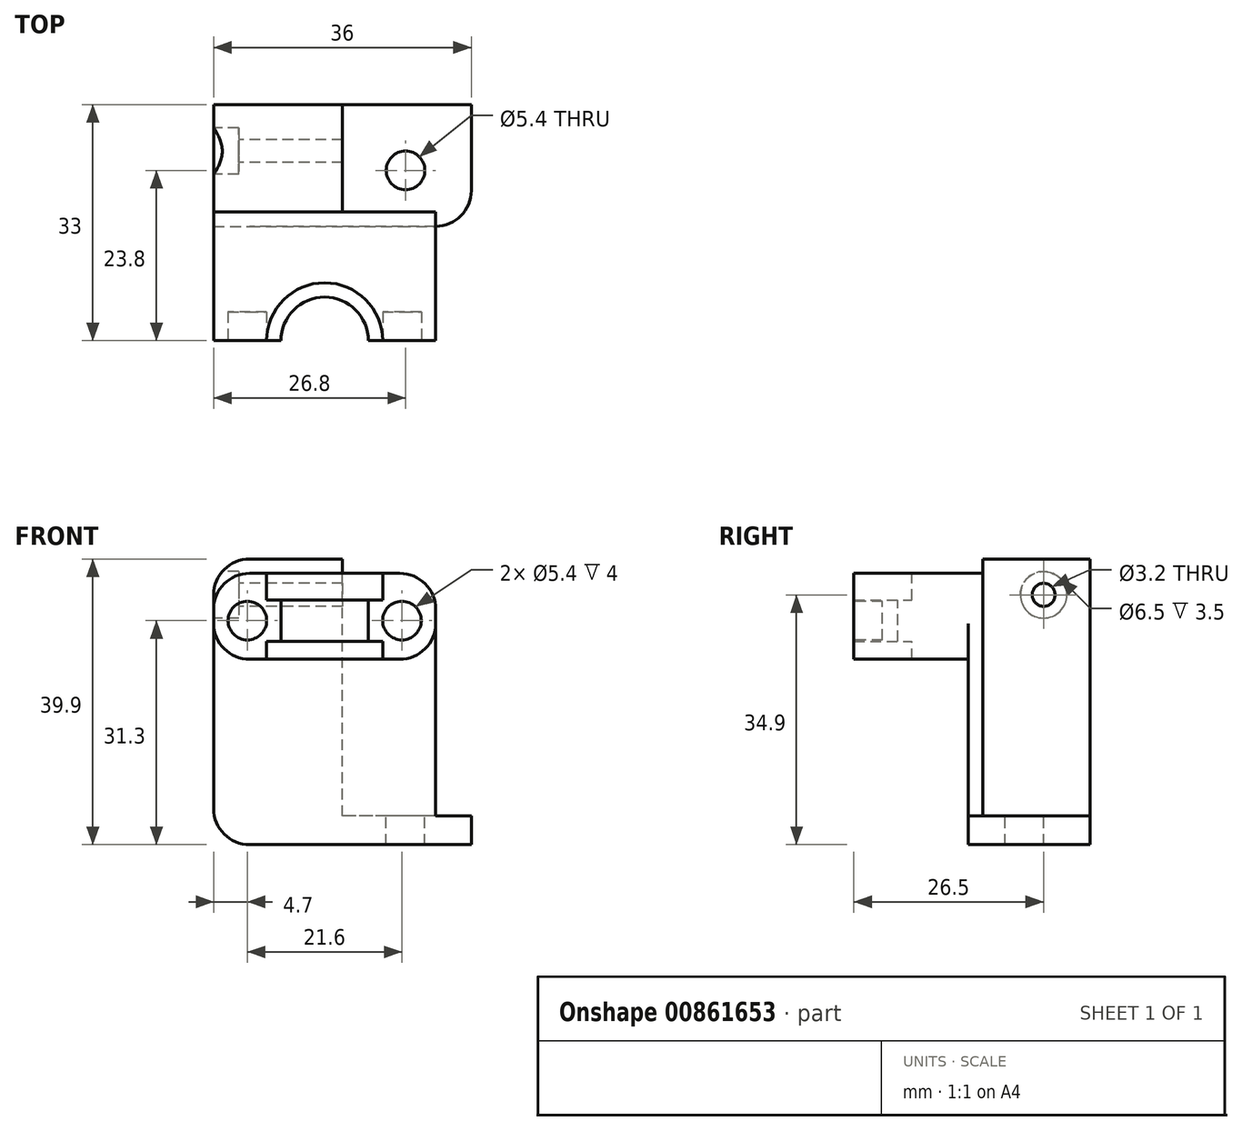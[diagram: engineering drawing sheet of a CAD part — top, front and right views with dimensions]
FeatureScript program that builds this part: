
annotation { "Feature Type Name" : "Feature", "Feature Type Description" : "" }
export const myFeature = defineFeature(function(context is Context, id is Id, definition is map)
    precondition{}
    {
        {
            var Q0;
            Q0=qCreatedBy(makeId("Front.planeOp"),FACE);
            var sketch = newSketch(context, id + "F0", { "sketchPlane" : qUnion([Q0])});
            skLineSegment(sketch, "E0", {"start": v(0, 35.9) * mm, "end": v(-18, 35.9) * mm});
            skLineSegment(sketch, "E1", {"start": v(-18, 35.9) * mm, "end": v(-18, -4) * mm});
            skLineSegment(sketch, "E2", {"start": v(-18, -4) * mm, "end": v(18, -4) * mm});
            skLineSegment(sketch, "E3", {"start": v(18, -4) * mm, "end": v(18, 0) * mm});
            skLineSegment(sketch, "E4", {"start": v(18, 0) * mm, "end": v(0, 0) * mm});
            skLineSegment(sketch, "E5", {"start": v(0, 0) * mm, "end": v(0, 35.9) * mm});
            skSolve(sketch);
        }
        {
            var Q0;
            Q0 = qSketchRegion(id + "F0", true);
            extrude(context, id + "F1", {"entities" : qUnion([Q0]), "depth" : 15 * mm, "offsetDistance" : 25 * mm});
        }
        {
            var Q0;
            Q0=makeQuery(id+"F1.opExtrude","SWEPT_FACE",FACE,{"disambiguationData":[OSD([sQuery(id+"F0.wireOp",EDGE,"E1")])]});
            var sketch = newSketch(context, id + "F2", { "sketchPlane" : qUnion([Q0])});
            skCircle(sketch, "E6", {"center": v(6.5, 30.9) * mm, "radius": 1.6 * mm});
            skSolve(sketch);
        }
        {
            var Q0;
            Q0 = qSketchRegion(id + "F2", true);
            extrude(context, id + "F3", {"entities" : qUnion([Q0]), "operationType" : NewBodyOperationType.REMOVE, "endBound" : BoundingType.THROUGH_ALL, "oppositeDirection" : true, "depth" : 25 * mm, "offsetDistance" : 25 * mm});
        }
        {
            var Q0;
            Q0=makeQuery(id+"F1.opExtrude","SWEPT_FACE",FACE,{"disambiguationData":[OSD([sQuery(id+"F0.wireOp",EDGE,"E4")])]});
            var sketch = newSketch(context, id + "F4", { "sketchPlane" : qUnion([Q0])});
            skCircle(sketch, "E7", {"center": v(8.8, -9.2) * mm, "radius": 2.7 * mm});
            skSolve(sketch);
        }
        {
            var Q0;
            Q0 = qSketchRegion(id + "F4", true);
            extrude(context, id + "F5", {"entities" : qUnion([Q0]), "operationType" : NewBodyOperationType.REMOVE, "oppositeDirection" : true, "depth" : 25 * mm, "offsetDistance" : 25 * mm});
        }
        {
            var Q0;
            Q0=makeQuery(id+"F1.opExtrude","SWEPT_FACE",FACE,{"disambiguationData":[OSD([sQuery(id+"F0.wireOp",EDGE,"E0")])]});
            cPlane(context, id + "F6", {"entities" : qUnion([Q0]), "cplaneType" : CPlaneType.OFFSET, "offset" : 2 * mm, "oppositeDirection" : true, "width" : 150 * mm, "height" : 150 * mm});
        }
        {
            var Q0;
            Q0=qCreatedBy(id+"F6.planeOp",FACE);
            var sketch = newSketch(context, id + "F7", { "sketchPlane" : qUnion([Q0])});
            skCircle(sketch, "E8", {"center": v(-2.5, -33) * mm, "radius": 6 * mm, "construction": true});
            skArc(sketch, "E9", {"start": v(5.5, -33) * mm, "mid": v(-2.5, -25) * mm, "end": v(-10.5, -33) * mm, "construction": true});
            skLineSegment(sketch, "E10", {"start": v(-2.5, -33) * mm, "end": v(-2.5, 0) * mm, "construction": true});
            skLineSegment(sketch, "E11.bottom", {"start": v(-16.5, -33) * mm, "end": v(-10.5, -33) * mm, "construction": true});
            skLineSegment(sketch, "E11.top", {"start": v(-16.5, -29.2) * mm, "end": v(-10.5, -29.2) * mm, "construction": true});
            skLineSegment(sketch, "E11.left", {"start": v(-16.5, -33) * mm, "end": v(-16.5, -29.2) * mm, "construction": true});
            skLineSegment(sketch, "E11.right", {"start": v(-10.5, -33) * mm, "end": v(-10.5, -29.2) * mm, "construction": true});
            skLineSegment(sketch, "E12.MirrorCS", {"start": v(11.5, -29.2) * mm, "end": v(5.5, -29.2) * mm, "construction": true});
            skLineSegment(sketch, "E13.MirrorCS", {"start": v(11.5, -33) * mm, "end": v(11.5, -29.2) * mm, "construction": true});
            skLineSegment(sketch, "E14.MirrorCS", {"start": v(11.5, -33) * mm, "end": v(5.5, -33) * mm, "construction": true});
            skLineSegment(sketch, "E15.MirrorCS", {"start": v(5.5, -33) * mm, "end": v(5.5, -29.2) * mm, "construction": true});
            skLineSegment(sketch, "E16", {"start": v(-18, -15) * mm, "end": v(-18, -33) * mm});
            skLineSegment(sketch, "E17", {"start": v(-18, -33) * mm, "end": v(-10.5, -33) * mm});
            skLineSegment(sketch, "E18", {"start": v(5.5, -33) * mm, "end": v(13, -33) * mm});
            skLineSegment(sketch, "E19", {"start": v(13, -33) * mm, "end": v(13, -15) * mm});
            skLineSegment(sketch, "E20", {"start": v(13, -15) * mm, "end": v(-18, -15) * mm});
            skArc(sketch, "E21", {"start": v(5.6, -33) * mm, "mid": v(-2.5, -24.9) * mm, "end": v(-10.6, -33) * mm});
            skSolve(sketch);
        }
        {
            var Q0;
            Q0 = qSketchRegion(id + "F7", true);
            extrude(context, id + "F8", {"entities" : qUnion([Q0]), "operationType" : NewBodyOperationType.ADD, "oppositeDirection" : true, "depth" : 3.7 * mm, "offsetDistance" : 25 * mm});
        }
        {
            var Q0;
            Q0=makeQuery(id+"F8.opExtrude","CAP_FACE",FACE,{"disambiguationData":[OSD([sQuery(id+"F7.wireOp",EDGE,"E16"),sQuery(id+"F7.wireOp",EDGE,"E17"),sQuery(id+"F7.wireOp",EDGE,"E18"),sQuery(id+"F7.wireOp",EDGE,"E19"),sQuery(id+"F7.wireOp",EDGE,"E20"),sQuery(id+"F7.wireOp",EDGE,"E21")])],"isStart":false});
            var sketch = newSketch(context, id + "F9", { "sketchPlane" : qUnion([Q0])});
            skLineSegment(sketch, "E22.0.0", {"start": v(13, 15) * mm, "end": v(13, 33) * mm});
            skLineSegment(sketch, "E22.0.1", {"start": v(13, 33) * mm, "end": v(5.6, 33) * mm});
            skLineSegment(sketch, "E22.0.3", {"start": v(-10.6, 33) * mm, "end": v(-18, 33) * mm});
            skLineSegment(sketch, "E22.0.4", {"start": v(-18, 33) * mm, "end": v(-18, 15) * mm});
            skLineSegment(sketch, "E22.0.5", {"start": v(-18, 15) * mm, "end": v(0, 15) * mm});
            skLineSegment(sketch, "E22.0.6", {"start": v(0, 15) * mm, "end": v(13, 15) * mm});
            skArc(sketch, "E23", {"start": v(-8.6, 33) * mm, "mid": v(-2.5, 26.9) * mm, "end": v(3.6, 33) * mm});
            skLineSegment(sketch, "E24", {"start": v(-10.6, 33) * mm, "end": v(-8.6, 33) * mm});
            skLineSegment(sketch, "E25", {"start": v(3.6, 33) * mm, "end": v(5.6, 33) * mm});
            skSolve(sketch);
        }
        {
            var Q0;
            Q0 = qSketchRegion(id + "F9", true);
            extrude(context, id + "F10", {"entities" : qUnion([Q0]), "operationType" : NewBodyOperationType.ADD, "depth" : 5.8 * mm, "offsetDistance" : 25 * mm});
        }
        {
            var Q0;
            Q0=makeQuery(id+"F10.opExtrude","CAP_FACE",FACE,{"disambiguationData":[OSD([sQuery(id+"F9.wireOp",EDGE,"E22.0.0"),sQuery(id+"F9.wireOp",EDGE,"E22.0.1"),sQuery(id+"F9.wireOp",EDGE,"E22.0.3"),sQuery(id+"F9.wireOp",EDGE,"E22.0.4"),sQuery(id+"F9.wireOp",EDGE,"E22.0.5"),sQuery(id+"F9.wireOp",EDGE,"E22.0.6"),sQuery(id+"F9.wireOp",EDGE,"E23"),sQuery(id+"F9.wireOp",EDGE,"E24"),sQuery(id+"F9.wireOp",EDGE,"E25")])],"isStart":false});
            var sketch = newSketch(context, id + "F11", { "sketchPlane" : qUnion([Q0])});
            skLineSegment(sketch, "E26.0.0", {"start": v(13, 33) * mm, "end": v(13, 15) * mm});
            skLineSegment(sketch, "E26.0.1", {"start": v(13, 15) * mm, "end": v(-18, 15) * mm});
            skLineSegment(sketch, "E26.0.2", {"start": v(-18, 15) * mm, "end": v(-18, 15) * mm});
            skLineSegment(sketch, "E26.0.3", {"start": v(-18, 15) * mm, "end": v(-18, 33) * mm});
            skLineSegment(sketch, "E26.0.4", {"start": v(-18, 33) * mm, "end": v(-10.6, 33) * mm});
            skArc(sketch, "E26.0.5", {"start": v(-10.6, 33) * mm, "mid": v(-2.5, 24.9) * mm, "end": v(5.6, 33) * mm});
            skLineSegment(sketch, "E26.0.6", {"start": v(5.6, 33) * mm, "end": v(13, 33) * mm});
            skSolve(sketch);
        }
        {
            var Q0;
            Q0 = qSketchRegion(id + "F11", true);
            extrude(context, id + "F12", {"entities" : qUnion([Q0]), "operationType" : NewBodyOperationType.ADD, "depth" : 2.5 * mm, "offsetDistance" : 25 * mm});
        }
        {
            var Q0;
            Q0=makeQuery(id+"F12.boolean.opBoolean","MERGE",FACE,{"derivedFrom":[makeQuery(id+"F10.boolean.opBoolean","MERGE",FACE,{"derivedFrom":[makeQuery(id+"F8.opExtrude","SWEPT_FACE",FACE,{"disambiguationData":[OSD([sQuery(id+"F7.wireOp",EDGE,"E17")])]}),makeQuery(id+"F10.opExtrude","SWEPT_FACE",FACE,{"disambiguationData":[OSD([sQuery(id+"F9.wireOp",EDGE,"E22.0.3"),sQuery(id+"F9.wireOp",EDGE,"E24")])]})]}),makeQuery(id+"F12.opExtrude","SWEPT_FACE",FACE,{"disambiguationData":[OSD([sQuery(id+"F11.wireOp",EDGE,"E26.0.4")])]})]});
            var sketch = newSketch(context, id + "F13", { "sketchPlane" : qUnion([Q0])});
            skLineSegment(sketch, "E27", {"start": v(-8.6, 27.3) * mm, "end": v(-13.3, 27.3) * mm, "construction": true});
            skCircle(sketch, "E28", {"center": v(-13.3, 27.3) * mm, "radius": 2.7 * mm});
            skPoint(sketch, "E29", {"position": v(-10.6, 27.3) * mm});
            skLineSegment(sketch, "E30.0", {"start": v(3.6, 30.2) * mm, "end": v(-8.6, 30.2) * mm, "construction": true});
            skLineSegment(sketch, "E31", {"start": v(-2.5, 30.2) * mm, "end": v(-2.5, 25.4) * mm, "construction": true});
            skCircle(sketch, "E32.MirrorC", {"center": v(8.3, 27.3) * mm, "radius": 2.7 * mm});
            skSolve(sketch);
        }
        {
            var Q0;
            Q0 = qSketchRegion(id + "F13", true);
            extrude(context, id + "F14", {"entities" : qUnion([Q0]), "operationType" : NewBodyOperationType.REMOVE, "oppositeDirection" : true, "depth" : 4 * mm, "offsetDistance" : 25 * mm});
        }
        {
            var Q0;
            Q0=makeQuery(id+"F12.boolean.opBoolean","MERGE",FACE,{"derivedFrom":[makeQuery(id+"F10.boolean.opBoolean","MERGE",FACE,{"derivedFrom":[makeQuery(id+"F8.boolean.opBoolean","MERGE",FACE,{"derivedFrom":[makeQuery(id+"F1.opExtrude","SWEPT_FACE",FACE,{"disambiguationData":[OSD([sQuery(id+"F0.wireOp",EDGE,"E1")])]}),makeQuery(id+"F8.opExtrude","SWEPT_FACE",FACE,{"disambiguationData":[OSD([sQuery(id+"F7.wireOp",EDGE,"E16")])]})]}),makeQuery(id+"F10.opExtrude","SWEPT_FACE",FACE,{"disambiguationData":[OSD([sQuery(id+"F9.wireOp",EDGE,"E22.0.4")])]})]}),makeQuery(id+"F12.opExtrude","SWEPT_FACE",FACE,{"disambiguationData":[OSD([sQuery(id+"F11.wireOp",EDGE,"E26.0.3")])]})]});
            var sketch = newSketch(context, id + "F15", { "sketchPlane" : qUnion([Q0])});
            skCircle(sketch, "E33", {"center": v(6.5, 30.9) * mm, "radius": 3.25 * mm});
            skSolve(sketch);
        }
        {
            var Q0;
            Q0 = qSketchRegion(id + "F15", true);
            extrude(context, id + "F16", {"entities" : qUnion([Q0]), "operationType" : NewBodyOperationType.REMOVE, "oppositeDirection" : true, "depth" : 3.5 * mm, "offsetDistance" : 25 * mm});
        }
        {
            var Q0;
            Q0=makeQuery(id+"F12.opExtrude","CAP_FACE",FACE,{"disambiguationData":[OSD([sQuery(id+"F11.wireOp",EDGE,"E26.0.0"),sQuery(id+"F11.wireOp",EDGE,"E26.0.1"),sQuery(id+"F11.wireOp",EDGE,"E26.0.2"),sQuery(id+"F11.wireOp",EDGE,"E26.0.3"),sQuery(id+"F11.wireOp",EDGE,"E26.0.4"),sQuery(id+"F11.wireOp",EDGE,"E26.0.5"),sQuery(id+"F11.wireOp",EDGE,"E26.0.6")])],"isStart":false});
            var sketch = newSketch(context, id + "F17", { "sketchPlane" : qUnion([Q0])});
            skLineSegment(sketch, "E34.bottom", {"start": v(-18, 15) * mm, "end": v(13, 15) * mm});
            skLineSegment(sketch, "E34.top", {"start": v(-18, 17) * mm, "end": v(13, 17) * mm});
            skLineSegment(sketch, "E34.left", {"start": v(-18, 15) * mm, "end": v(-18, 17) * mm});
            skLineSegment(sketch, "E34.right", {"start": v(13, 15) * mm, "end": v(13, 17) * mm});
            skSolve(sketch);
        }
        {
            var Q0;
            Q0 = qSketchRegion(id + "F17", true);
            var Q1;
            Q1=makeQuery(id+"F1.opExtrude","SWEPT_FACE",FACE,{"disambiguationData":[OSD([sQuery(id+"F0.wireOp",EDGE,"E2")])]});
            extrude(context, id + "F18", {"entities" : qUnion([Q0]), "operationType" : NewBodyOperationType.ADD, "endBound" : BoundingType.UP_TO_SURFACE, "depth" : 25 * mm, "endBoundEntityFace" : qUnion([Q1]), "offsetDistance" : 25 * mm});
        }
        {
            var Q0;
            Q0=makeQuery(id+"F1.opExtrude","CAP_FACE",FACE,{"disambiguationData":[OSD([sQuery(id+"F0.wireOp",EDGE,"E0"),sQuery(id+"F0.wireOp",EDGE,"E1"),sQuery(id+"F0.wireOp",EDGE,"E2"),sQuery(id+"F0.wireOp",EDGE,"E3"),sQuery(id+"F0.wireOp",EDGE,"E4"),sQuery(id+"F0.wireOp",EDGE,"E5")])],"isStart":false});
            var sketch = newSketch(context, id + "F19", { "sketchPlane" : qUnion([Q0])});
            skLineSegment(sketch, "E35.0.0", {"start": v(13, 0) * mm, "end": v(13, -4) * mm});
            skLineSegment(sketch, "E35.0.1", {"start": v(13, -4) * mm, "end": v(18, -4) * mm});
            skLineSegment(sketch, "E35.0.2", {"start": v(18, -4) * mm, "end": v(18, 0) * mm});
            skLineSegment(sketch, "E35.0.3", {"start": v(18, 0) * mm, "end": v(13, 0) * mm});
            skSolve(sketch);
        }
        {
            var Q0;
            Q0 = qSketchRegion(id + "F19", true);
            var Q1;
            Q1=makeQuery(id+"F18.opExtrude","SWEPT_FACE",FACE,{"disambiguationData":[OSD([sQuery(id+"F17.wireOp",EDGE,"E34.top")])]});
            extrude(context, id + "F20", {"entities" : qUnion([Q0]), "operationType" : NewBodyOperationType.ADD, "endBound" : BoundingType.UP_TO_SURFACE, "depth" : 25 * mm, "endBoundEntityFace" : qUnion([Q1]), "offsetDistance" : 25 * mm});
        }
        {
            var Q0;
            Q0=makeQuery(id+"F12.opExtrude","CAP_EDGE",EDGE,{"disambiguationData":[OSD([sQuery(id+"F11.wireOp",EDGE,"E26.0.3")])],"isStart":false});
            var Q1;
            Q1=makeQuery(id+"F8.opExtrude","CAP_EDGE",EDGE,{"disambiguationData":[OSD([sQuery(id+"F7.wireOp",EDGE,"E19")])],"isStart":true});
            var Q2;
            Q2=makeQuery(id+"F12.opExtrude","CAP_EDGE",EDGE,{"disambiguationData":[OSD([sQuery(id+"F11.wireOp",EDGE,"E26.0.0")])],"isStart":false});
            var Q3;
            Q3=makeQuery(id+"F18.boolean.opBoolean","MERGE",EDGE,{"derivedFrom":[makeQuery(id+"F1.opExtrude","SWEPT_EDGE",EDGE,{"disambiguationData":[OSD([sQuery(id+"F0.wireOp",EDGE,"E1"),sQuery(id+"F0.wireOp",EDGE,"E2")])]}),makeQuery(id+"F18.opExtrude","CAP_EDGE",EDGE,{"disambiguationData":[OSD([sQuery(id+"F17.wireOp",EDGE,"E34.left")])],"isStart":false})]});
            var Q4;
            Q4=makeQuery(id+"F20.opExtrude","CAP_EDGE",EDGE,{"disambiguationData":[OSD([sQuery(id+"F19.wireOp",EDGE,"E35.0.2")])],"isStart":false});
            var Q5;
            Q5=makeQuery(id+"F8.opExtrude","CAP_EDGE",EDGE,{"disambiguationData":[OSD([sQuery(id+"F7.wireOp",EDGE,"E16")])],"isStart":true});
            fillet(context, id + "F21", {"entities" : qUnion([Q0, Q1, Q2, Q3, Q4, Q5]), "radius" : 5 * mm, "tangentPropagation" : true, "allowEdgeOverflow" : false});
        }
        {
            var Q0;
            Q0=makeQuery(id+"F1.opExtrude","SWEPT_EDGE",EDGE,{"disambiguationData":[OSD([sQuery(id+"F0.wireOp",EDGE,"E0"),sQuery(id+"F0.wireOp",EDGE,"E1")])]});
            fillet(context, id + "F22", {"entities" : qUnion([Q0]), "radius" : 5 * mm, "tangentPropagation" : true, "allowEdgeOverflow" : false});
        }
    });
